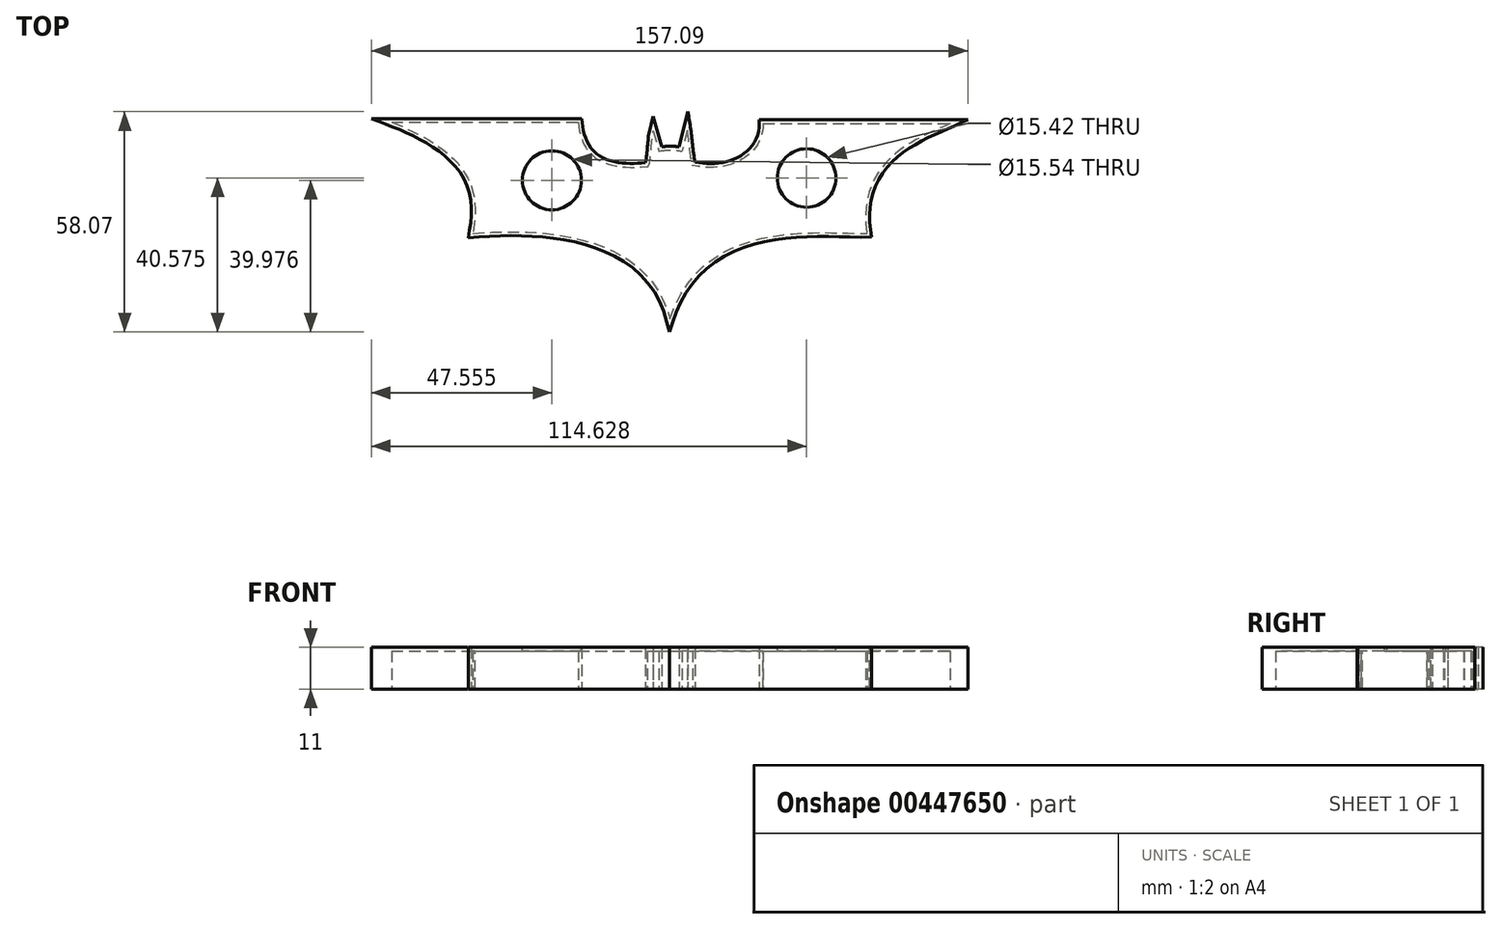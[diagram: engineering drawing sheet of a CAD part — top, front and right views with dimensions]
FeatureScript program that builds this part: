
annotation { "Feature Type Name" : "Feature", "Feature Type Description" : "" }
export const myFeature = defineFeature(function(context is Context, id is Id, definition is map)
    precondition{}
    {
        {
            var Q0;
            Q0=qCreatedBy(makeId("Top.planeOp"),FACE);
            var sketch = newSketch(context, id + "F0", { "sketchPlane" : qUnion([Q0])});
            skLineSegment(sketch, "E0", {"start": v(-73.29, 22.75) * mm, "end": v(-24.14, 22.75) * mm});
            skLineSegment(sketch, "E1", {"start": v(24.52, 22.45) * mm, "end": v(73.85, 22.45) * mm});
            skFitSpline(sketch, "E2", {"points": [v(73.85, 22.45) * mm, v(51.9, -6.48) * mm], "startDerivative": vector(-23.93, -10.9) * mm, "endDerivative": vector(9.08, -58.56) * mm});
            skFitSpline(sketch, "E3", {"points": [v(-24.14, 22.75) * mm, v(-6.02, 11.15) * mm], "startDerivative": vector(2.54, -26.28) * mm, "endDerivative": vector(36.12, 3.92) * mm});
            skFitSpline(sketch, "E4", {"points": [v(-6.02, 11.15) * mm, v(-4.38, 20.5) * mm], "startDerivative": vector(3.2, -1.59) * mm, "endDerivative": vector(2, 7.72) * mm});
            skLineSegment(sketch, "E5", {"start": v(-4.38, 20.5) * mm, "end": v(-2.9, 15.2) * mm});
            skLineSegment(sketch, "E6", {"start": v(4.52, 20.6) * mm, "end": v(3.13, 15.15) * mm});
            skFitSpline(sketch, "E7", {"points": [v(-2.9, 15.2) * mm, v(3.13, 15.15) * mm], "startDerivative": vector(6.64, 0.93) * mm, "endDerivative": vector(5.96, -1.3) * mm});
            skFitSpline(sketch, "E8", {"points": [v(-73.29, 22.75) * mm, v(-51.9, -6.52) * mm], "startDerivative": vector(67.06, -26) * mm, "endDerivative": vector(-5.36, -30.08) * mm});
            skFitSpline(sketch, "E9", {"points": [v(-51.9, -6.52) * mm, v(0, -28.97) * mm], "startDerivative": vector(121.53, 10) * mm, "endDerivative": vector(7.18, -27.58) * mm});
            skFitSpline(sketch, "E10", {"points": [v(0, -28.97) * mm, v(51.9, -6.48) * mm], "startDerivative": vector(27.64, 83.24) * mm, "endDerivative": vector(30.9, 1.7) * mm});
            skFitSpline(sketch, "E11", {"points": [v(4.52, 20.6) * mm, v(5.96, 11.37) * mm], "startDerivative": vector(1.44, -9.24) * mm, "endDerivative": vector(2.12, -2.82) * mm});
            skFitSpline(sketch, "E12", {"points": [v(24.52, 22.45) * mm, v(5.96, 11.37) * mm], "startDerivative": vector(0.33, -22.57) * mm, "endDerivative": vector(-33.15, 6.7) * mm});
            skSolve(sketch);
        }
        {
            var Q0;
            Q0=makeQuery(id+"F0.imprint","IMPRINT",FACE,{"disambiguationData":[TD([[makeQuery(id+"F0.imprint","IMPRINT",EDGE,{"derivedFrom":sQuery(id+"F0.wireOp",EDGE,"E0")}),-1.0]])]});
            extrude(context, id + "F1", {"entities" : qUnion([Q0]), "depth" : 10 * mm});
        }
        {
            var Q0;
            Q0=makeQuery(id+"F1.opExtrude","CAP_FACE",FACE,{"disambiguationData":[OSD([sQuery(id+"F0.wireOp",EDGE,"E0"),sQuery(id+"F0.wireOp",EDGE,"E1"),sQuery(id+"F0.wireOp",EDGE,"E2"),sQuery(id+"F0.wireOp",EDGE,"E3"),sQuery(id+"F0.wireOp",EDGE,"E4"),sQuery(id+"F0.wireOp",EDGE,"E5"),sQuery(id+"F0.wireOp",EDGE,"E6"),sQuery(id+"F0.wireOp",EDGE,"E7"),sQuery(id+"F0.wireOp",EDGE,"E8"),sQuery(id+"F0.wireOp",EDGE,"E9"),sQuery(id+"F0.wireOp",EDGE,"E10"),sQuery(id+"F0.wireOp",EDGE,"E11"),sQuery(id+"F0.wireOp",EDGE,"E12")])],"isStart":true});
            shell(context, id + "F2", {"entities" : qUnion([Q0]), "thickness" : 1 * mm, "oppositeDirection" : true});
        }
        {
            var Q0;
            Q0=makeQuery(id+"F1.opExtrude","CAP_FACE",FACE,{"disambiguationData":[OSD([sQuery(id+"F0.wireOp",EDGE,"E0"),sQuery(id+"F0.wireOp",EDGE,"E1"),sQuery(id+"F0.wireOp",EDGE,"E2"),sQuery(id+"F0.wireOp",EDGE,"E3"),sQuery(id+"F0.wireOp",EDGE,"E4"),sQuery(id+"F0.wireOp",EDGE,"E5"),sQuery(id+"F0.wireOp",EDGE,"E6"),sQuery(id+"F0.wireOp",EDGE,"E7"),sQuery(id+"F0.wireOp",EDGE,"E8"),sQuery(id+"F0.wireOp",EDGE,"E9"),sQuery(id+"F0.wireOp",EDGE,"E10"),sQuery(id+"F0.wireOp",EDGE,"E11"),sQuery(id+"F0.wireOp",EDGE,"E12")])],"isStart":false});
            var sketch = newSketch(context, id + "F3", { "sketchPlane" : qUnion([Q0])});
            skCircle(sketch, "E13", {"center": v(-31.07, 7.49) * mm, "radius": 7.77 * mm});
            skCircle(sketch, "E14", {"center": v(36, 8.08) * mm, "radius": 7.7 * mm});
            skSolve(sketch);
        }
        {
            var Q0;
            Q0=makeQuery(id+"F3.imprint","IMPRINT",FACE,{"disambiguationData":[TD([[makeQuery(id+"F3.imprint","IMPRINT",EDGE,{"derivedFrom":sQuery(id+"F3.wireOp",EDGE,"E13")}),1.0]])]});
            var Q1;
            Q1=makeQuery(id+"F3.imprint","IMPRINT",FACE,{"disambiguationData":[TD([[makeQuery(id+"F3.imprint","IMPRINT",EDGE,{"derivedFrom":sQuery(id+"F3.wireOp",EDGE,"E14")}),1.0]])]});
            extrude(context, id + "F4", {"entities" : qUnion([Q0, Q1]), "operationType" : NewBodyOperationType.REMOVE, "oppositeDirection" : true, "depth" : 10 * mm});
        }
    });
